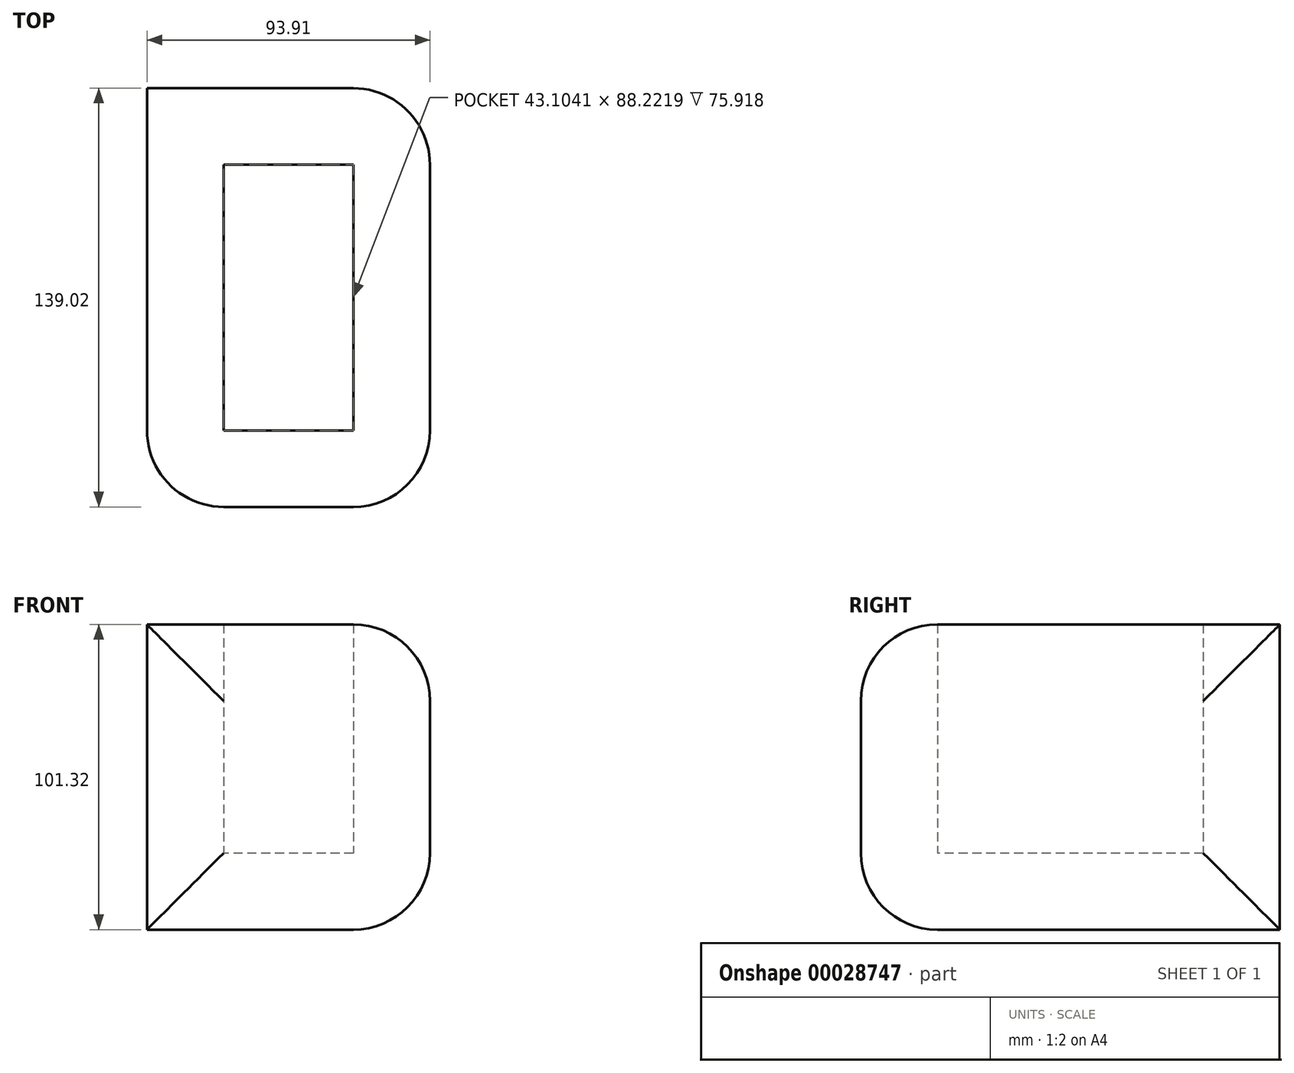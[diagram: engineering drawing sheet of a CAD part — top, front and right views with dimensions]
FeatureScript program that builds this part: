
annotation { "Feature Type Name" : "Feature", "Feature Type Description" : "" }
export const myFeature = defineFeature(function(context is Context, id is Id, definition is map)
    precondition{}
    {
        {
            var Q0;
            Q0=qCreatedBy(makeId("Top.planeOp"),FACE);
            var sketch = newSketch(context, id + "F4", { "sketchPlane" : qUnion([Q0])});
            skLineSegment(sketch, "E0.bottom", {"start": v(44.4, 82.2) * mm, "end": v(-49.5, 82.2) * mm});
            skLineSegment(sketch, "E0.top", {"start": v(44.4, -56.83) * mm, "end": v(-49.5, -56.83) * mm});
            skLineSegment(sketch, "E0.left", {"start": v(44.4, 82.2) * mm, "end": v(44.4, -56.83) * mm});
            skLineSegment(sketch, "E0.right", {"start": v(-49.5, 82.2) * mm, "end": v(-49.5, -56.83) * mm});
            skSolve(sketch);
        }
        {
            var Q0;
            Q0=makeQuery(id+"F4.imprint","IMPRINT",FACE,{"disambiguationData":[TD([[makeQuery(id+"F4.imprint","IMPRINT",EDGE,{"derivedFrom":sQuery(id+"F4.wireOp",EDGE,"E0.bottom")}),1.0]])]});
            var sketch = newSketch(context, id + "F0", { "sketchPlane" : qUnion([Q0])});
            skSolve(sketch);
        }
        {
            var Q0;
            Q0 = qSketchRegion(id + "F0", true);
            var Q1;
            Q1=makeQuery(id+"F4.imprint","IMPRINT",FACE,{"disambiguationData":[TD([[makeQuery(id+"F4.imprint","IMPRINT",EDGE,{"derivedFrom":sQuery(id+"F4.wireOp",EDGE,"E0.bottom")}),1.0]])]});
            extrude(context, id + "F5", {"entities" : qUnion([Q0, Q1]), "depth" : 101.32 * mm});
        }
        {
            var Q0;
            Q0=makeQuery(id+"F5.opExtrude","SWEPT_FACE",FACE,{"disambiguationData":[OSD([sQuery(id+"F4.wireOp",EDGE,"E0.top")])]});
            var Q1;
            Q1=makeQuery(id+"F5.opExtrude","SWEPT_FACE",FACE,{"disambiguationData":[OSD([sQuery(id+"F4.wireOp",EDGE,"E0.left")])]});
            fillet(context, id + "F1", {"entities" : qUnion([Q0, Q1]), "radius" : 25.4 * mm, "tangentPropagation" : true, "allowEdgeOverflow" : false});
        }
        {
            var Q0;
            Q0=makeQuery(id+"F5.opExtrude","CAP_FACE",FACE,{"disambiguationData":[OSD([sQuery(id+"F4.wireOp",EDGE,"E0.bottom"),sQuery(id+"F4.wireOp",EDGE,"E0.top"),sQuery(id+"F4.wireOp",EDGE,"E0.left"),sQuery(id+"F4.wireOp",EDGE,"E0.right")])],"isStart":false});
            shell(context, id + "F2", {"entities" : qUnion([Q0]), "thickness" : 25.4 * mm});
        }
    });
